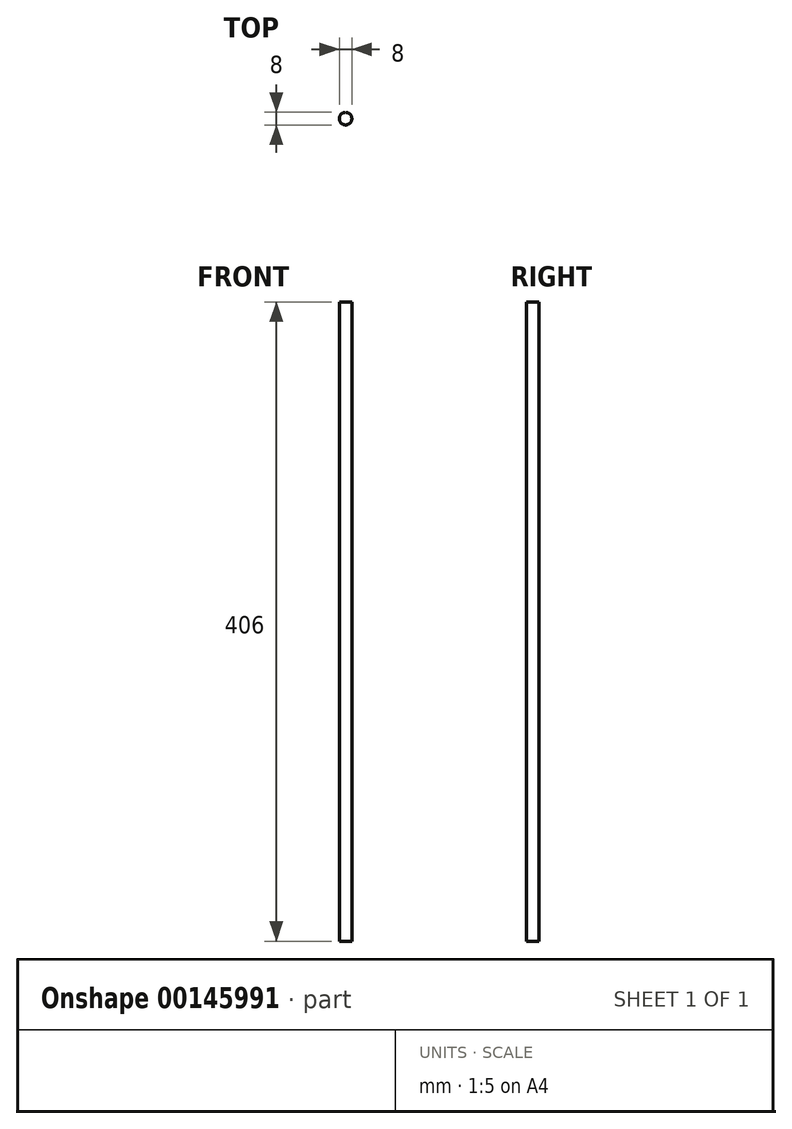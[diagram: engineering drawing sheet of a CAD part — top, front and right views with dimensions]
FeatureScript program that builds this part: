
annotation { "Feature Type Name" : "Feature", "Feature Type Description" : "" }
export const myFeature = defineFeature(function(context is Context, id is Id, definition is map)
    precondition{}
    {
        {
            var Q0;
            Q0=qCreatedBy(makeId("Top.planeOp"),FACE);
            var sketch = newSketch(context, id + "F0", { "sketchPlane" : qUnion([Q0])});
            skCircle(sketch, "E0", {"center": v(0, 0) * mm, "radius": 4 * mm});
            skSolve(sketch);
        }
        {
            var Q0;
            Q0 = qSketchRegion(id + "F0", true);
            extrude(context, id + "F1", {"entities" : qUnion([Q0]), "depth" : 406 * mm});
        }
    });
